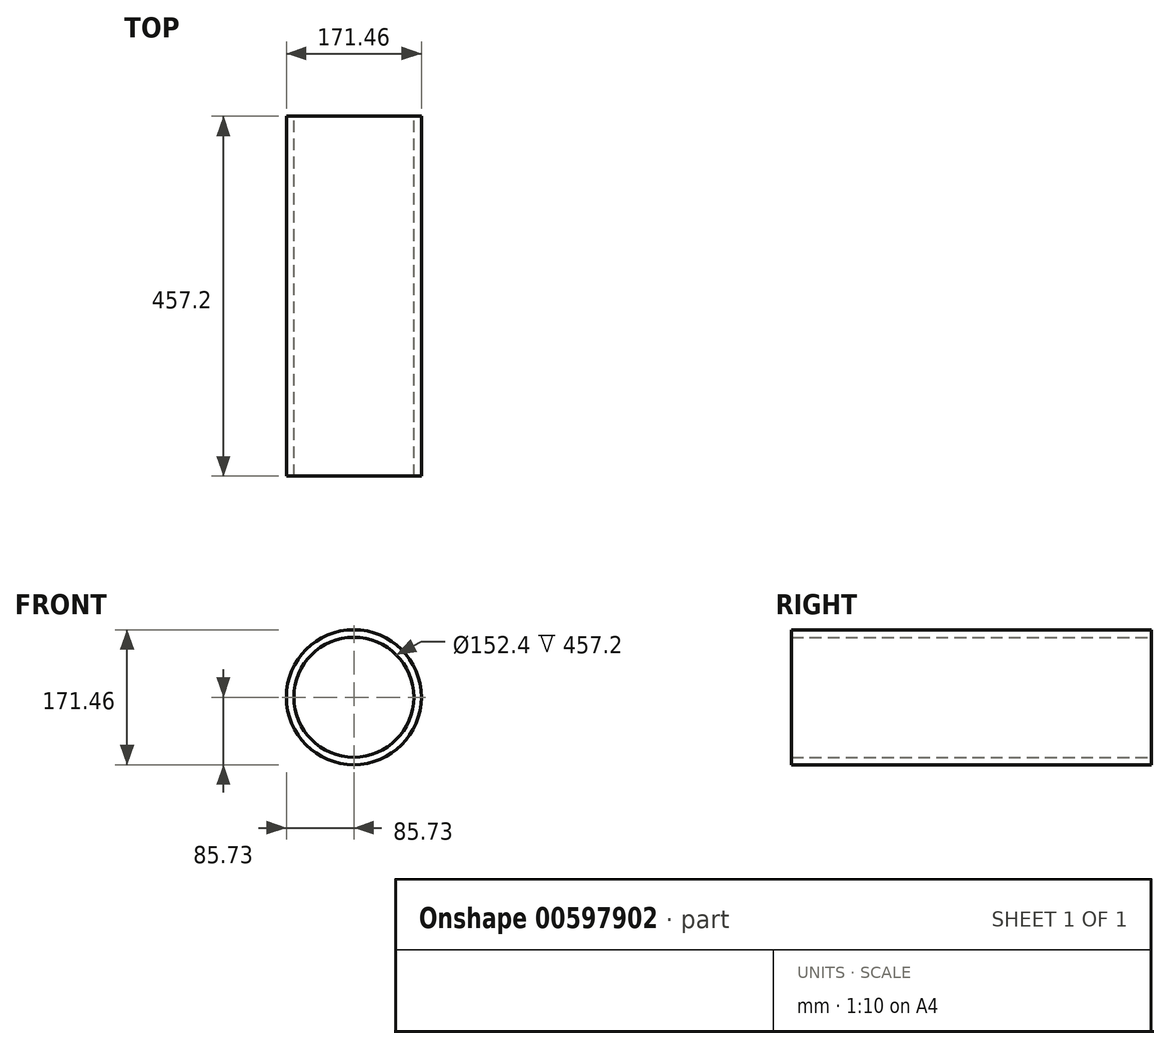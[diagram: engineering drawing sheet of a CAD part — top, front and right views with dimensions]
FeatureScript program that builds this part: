
annotation { "Feature Type Name" : "Feature", "Feature Type Description" : "" }
export const myFeature = defineFeature(function(context is Context, id is Id, definition is map)
    precondition{}
    {
        {
            var Q0;
            Q0=qCreatedBy(makeId("Front.planeOp"),FACE);
            var sketch = newSketch(context, id + "F0", { "sketchPlane" : qUnion([Q0])});
            skCircle(sketch, "E0", {"center": v(0, 0) * mm, "radius": 85.73 * mm});
            skCircle(sketch, "E1", {"center": v(0, 0) * mm, "radius": 76.2 * mm});
            skSolve(sketch);
        }
        {
            var Q0;
            Q0 = qSketchRegion(id + "F0", true);
            extrude(context, id + "F1", {"entities" : qUnion([Q0]), "depth" : 457.2 * mm, "offsetDistance" : 25.4 * mm});
        }
    });
